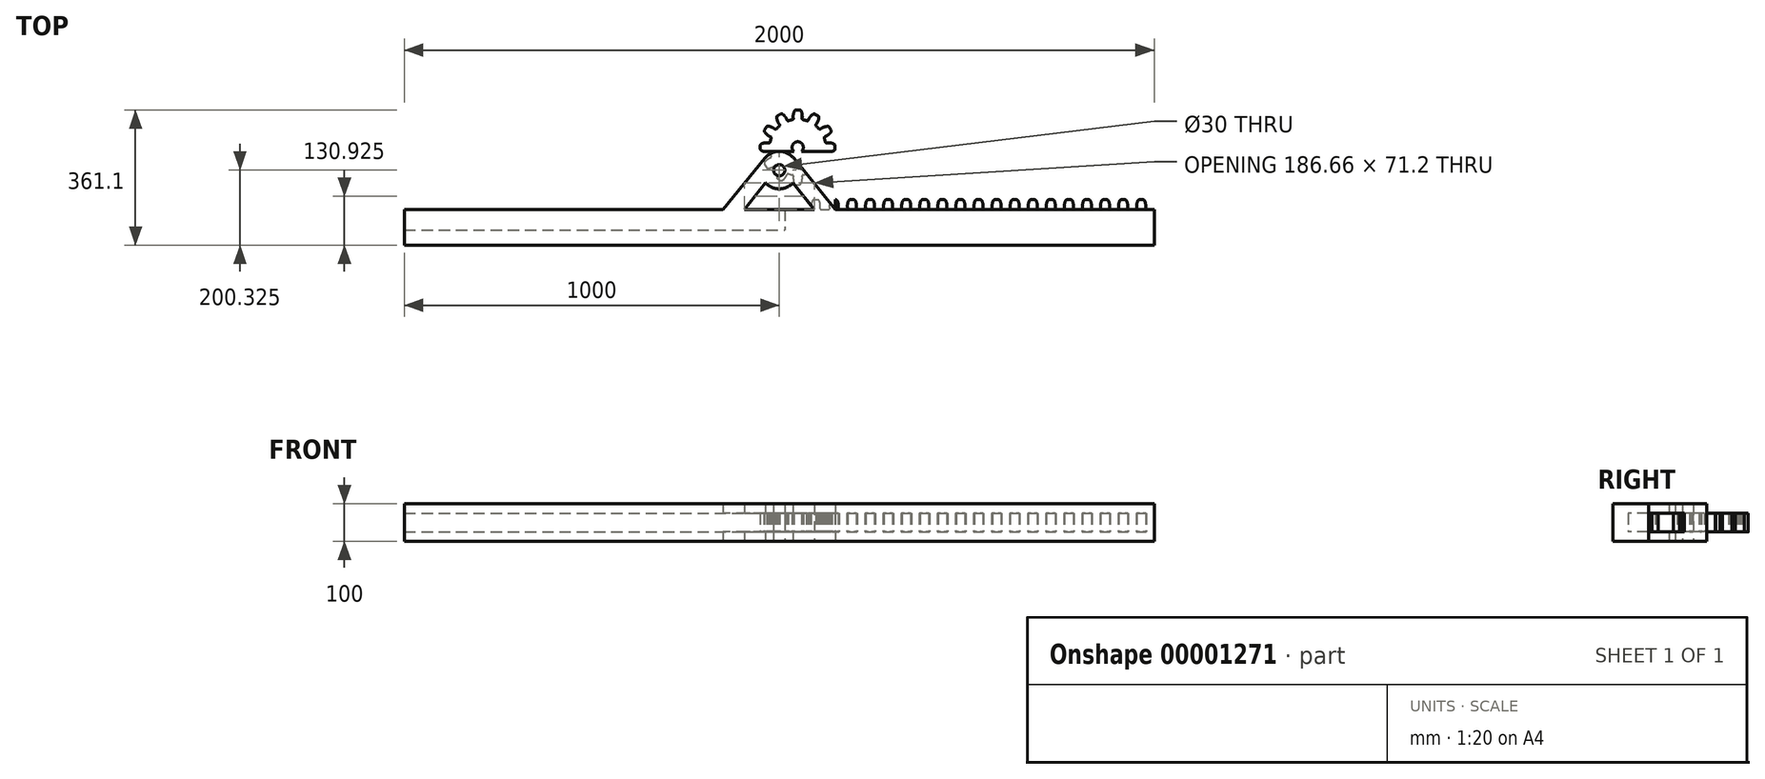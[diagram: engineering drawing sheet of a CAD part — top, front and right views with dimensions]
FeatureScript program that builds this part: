
annotation { "Feature Type Name" : "Feature", "Feature Type Description" : "" }
export const myFeature = defineFeature(function(context is Context, id is Id, definition is map)
    precondition{}
    {
        {
            var Q0;
            Q0=qCreatedBy(makeId("Top.planeOp"),FACE);
            var sketch = newSketch(context, id + "F0", { "sketchPlane" : qUnion([Q0])});
            skLineSegment(sketch, "E0", {"start": v(99.73, 0) * mm, "end": v(99.73, 4.1) * mm});
            skLineSegment(sketch, "E1", {"start": v(99.73, 4.1) * mm, "end": v(99.73, 0) * mm, "construction": true});
            skLineSegment(sketch, "E2", {"start": v(99.73, -4.64) * mm, "end": v(99.73, 0) * mm});
            skPoint(sketch, "E3.center", {"position": v(0, 0) * mm});
            skArc(sketch, "E4.0.MirrorCS", {"start": v(82.68, 12.2) * mm, "mid": v(90.04, 11.17) * mm, "end": v(97, 8.55) * mm});
            skArc(sketch, "E4.1.MirrorCS", {"start": v(76.7, 11.75) * mm, "mid": v(79.67, 12.26) * mm, "end": v(82.68, 12.2) * mm});
            skArc(sketch, "E5", {"start": v(73.52, 14.03) * mm, "mid": v(74.77, 12.37) * mm, "end": v(76.76, 11.75) * mm});
            skPoint(sketch, "E6.end.orphan", {"position": v(82.71, -12.06) * mm});
            skArc(sketch, "E7.0.MirrorCS", {"start": v(82.71, -12.06) * mm, "mid": v(89.87, -11.39) * mm, "end": v(96.73, -9.23) * mm});
            skArc(sketch, "E7.1.MirrorCS", {"start": v(76.73, -11.6) * mm, "mid": v(79.7, -12.11) * mm, "end": v(82.71, -12.06) * mm});
            skArc(sketch, "E7.2.MirrorCS", {"start": v(73.6, -13.73) * mm, "mid": v(74.87, -12.18) * mm, "end": v(76.79, -11.6) * mm});
            skLineSegment(sketch, "E8", {"start": v(-86.47, -119.82) * mm, "end": v(48.54, -119.82) * mm, "construction": true});
            skArc(sketch, "E9.2.MirrorCS", {"start": v(-13.73, -166.04) * mm, "mid": v(-12.2, -164.8) * mm, "end": v(-11.6, -162.91) * mm});
            skArc(sketch, "E9.7.MirrorCS", {"start": v(-12.06, -156.94) * mm, "mid": v(-11.39, -149.78) * mm, "end": v(-9.23, -142.92) * mm});
            skLineSegment(sketch, "E10", {"start": v(0, -139.92) * mm, "end": v(0, -175.01) * mm, "construction": true});
            skArc(sketch, "E11.1.MirrorCS", {"start": v(12.05, -156.94) * mm, "mid": v(11.38, -149.78) * mm, "end": v(9.22, -142.92) * mm});
            skArc(sketch, "E11.2.MirrorCS", {"start": v(13.72, -166.04) * mm, "mid": v(12.18, -164.78) * mm, "end": v(11.6, -162.86) * mm});
            skLineSegment(sketch, "E12", {"start": v(-4.64, -139.92) * mm, "end": v(4.64, -139.92) * mm});
            skArc(sketch, "E13.filletArc", {"start": v(-4.64, -139.92) * mm, "mid": v(-7.38, -140.73) * mm, "end": v(-9.23, -142.92) * mm});
            skArc(sketch, "E14.filletArc", {"start": v(9.22, -142.92) * mm, "mid": v(7.38, -140.73) * mm, "end": v(4.64, -139.92) * mm});
            skArc(sketch, "E15.trimOffspring", {"start": v(70.64, -24.92) * mm, "mid": v(72.37, -19.3) * mm, "end": v(73.67, -13.58) * mm});
            skLineSegment(sketch, "E16", {"start": v(-13.73, -166.04) * mm, "end": v(-34.8, -166.04) * mm});
            skLineSegment(sketch, "E17", {"start": v(950.75, -220.54) * mm, "end": v(-34.8, -220.54) * mm});
            skLineSegment(sketch, "E18", {"start": v(-34.8, -166.04) * mm, "end": v(-34.8, -220.54) * mm});
            skArc(sketch, "E19", {"start": v(-12.06, -156.94) * mm, "mid": v(-11.94, -159.93) * mm, "end": v(-11.6, -162.91) * mm});
            skPoint(sketch, "E11.0.MirrorCS.start.orphan", {"position": v(11.6, -162.91) * mm});
            skArc(sketch, "E20.0.MirrorCS", {"start": v(12.05, -156.94) * mm, "mid": v(11.94, -159.93) * mm, "end": v(11.6, -162.91) * mm});
            skPoint(sketch, "E21.0.MirrorP", {"position": v(-11.6, -162.91) * mm});
            skLineSegment(sketch, "E22", {"start": v(-12.06, -156.94) * mm, "end": v(12.05, -156.94) * mm, "construction": true});
            skLineSegment(sketch, "E23", {"start": v(12.05, -156.94) * mm, "end": v(36.17, -156.94) * mm, "construction": true});
            skLineSegment(sketch, "E24", {"start": v(13.72, -166.04) * mm, "end": v(34.5, -166.04) * mm});
            skPoint(sketch, "E25.visualSharp", {"position": v(99.73, 7) * mm});
            skArc(sketch, "E25.filletArc", {"start": v(99.73, 4.1) * mm, "mid": v(99, 6.7) * mm, "end": v(97, 8.55) * mm});
            skPoint(sketch, "E26.visualSharp", {"position": v(99.73, -7.74) * mm});
            skArc(sketch, "E26.filletArc", {"start": v(96.73, -9.23) * mm, "mid": v(98.91, -7.38) * mm, "end": v(99.73, -4.64) * mm});
            skArc(sketch, "E27.1.0.0", {"start": v(60.28, -156.94) * mm, "mid": v(60.16, -159.93) * mm, "end": v(59.83, -162.91) * mm});
            skLineSegment(sketch, "E27.1.0.1", {"start": v(61.95, -166.04) * mm, "end": v(82.72, -166.04) * mm});
            skArc(sketch, "E27.1.0.2", {"start": v(61.95, -166.04) * mm, "mid": v(60.4, -164.78) * mm, "end": v(59.83, -162.86) * mm});
            skArc(sketch, "E27.1.0.3", {"start": v(36.17, -156.94) * mm, "mid": v(36.28, -159.93) * mm, "end": v(36.62, -162.91) * mm});
            skArc(sketch, "E27.1.0.4", {"start": v(36.17, -156.94) * mm, "mid": v(36.84, -149.78) * mm, "end": v(39, -142.92) * mm});
            skArc(sketch, "E27.1.0.5", {"start": v(34.5, -166.04) * mm, "mid": v(36.03, -164.8) * mm, "end": v(36.62, -162.91) * mm});
            skArc(sketch, "E27.1.0.6", {"start": v(60.28, -156.94) * mm, "mid": v(59.6, -149.78) * mm, "end": v(57.44, -142.92) * mm});
            skPoint(sketch, "E27.1.0.7", {"position": v(36.62, -162.91) * mm});
            skLineSegment(sketch, "E27.1.0.8", {"start": v(43.58, -139.92) * mm, "end": v(52.86, -139.92) * mm});
            skArc(sketch, "E27.1.0.9", {"start": v(43.58, -139.92) * mm, "mid": v(40.84, -140.73) * mm, "end": v(39, -142.92) * mm});
            skPoint(sketch, "E27.1.0.10", {"position": v(59.83, -162.91) * mm});
            skArc(sketch, "E27.1.0.11", {"start": v(57.44, -142.92) * mm, "mid": v(55.6, -140.73) * mm, "end": v(52.86, -139.92) * mm});
            skArc(sketch, "E27.1.0.12", {"start": v(60.28, -156.94) * mm, "mid": v(60.16, -159.93) * mm, "end": v(59.83, -162.91) * mm});
            skArc(sketch, "E27.1.0.13", {"start": v(36.17, -156.94) * mm, "mid": v(36.84, -149.78) * mm, "end": v(39, -142.92) * mm});
            skArc(sketch, "E27.2.0.0", {"start": v(108.5, -156.94) * mm, "mid": v(108.39, -159.93) * mm, "end": v(108.05, -162.91) * mm});
            skLineSegment(sketch, "E27.2.0.1", {"start": v(110.17, -166.04) * mm, "end": v(130.94, -166.04) * mm});
            skArc(sketch, "E27.2.0.2", {"start": v(110.17, -166.04) * mm, "mid": v(108.62, -164.78) * mm, "end": v(108.05, -162.86) * mm});
            skArc(sketch, "E27.2.0.3", {"start": v(84.39, -156.94) * mm, "mid": v(84.5, -159.93) * mm, "end": v(84.84, -162.91) * mm});
            skArc(sketch, "E27.2.0.4", {"start": v(84.39, -156.94) * mm, "mid": v(85.06, -149.78) * mm, "end": v(87.22, -142.92) * mm});
            skArc(sketch, "E27.2.0.5", {"start": v(82.72, -166.04) * mm, "mid": v(84.25, -164.8) * mm, "end": v(84.84, -162.91) * mm});
            skArc(sketch, "E27.2.0.6", {"start": v(108.5, -156.94) * mm, "mid": v(107.83, -149.78) * mm, "end": v(105.67, -142.92) * mm});
            skPoint(sketch, "E27.2.0.7", {"position": v(84.84, -162.91) * mm});
            skLineSegment(sketch, "E27.2.0.8", {"start": v(91.8, -139.92) * mm, "end": v(101.09, -139.92) * mm});
            skArc(sketch, "E27.2.0.9", {"start": v(91.8, -139.92) * mm, "mid": v(89.07, -140.73) * mm, "end": v(87.22, -142.92) * mm});
            skPoint(sketch, "E27.2.0.10", {"position": v(108.05, -162.91) * mm});
            skArc(sketch, "E27.2.0.11", {"start": v(105.67, -142.92) * mm, "mid": v(103.82, -140.73) * mm, "end": v(101.09, -139.92) * mm});
            skArc(sketch, "E27.2.0.12", {"start": v(108.5, -156.94) * mm, "mid": v(108.39, -159.93) * mm, "end": v(108.05, -162.91) * mm});
            skArc(sketch, "E27.2.0.13", {"start": v(84.39, -156.94) * mm, "mid": v(85.06, -149.78) * mm, "end": v(87.22, -142.92) * mm});
            skArc(sketch, "E27.3.0.0", {"start": v(156.73, -156.94) * mm, "mid": v(156.61, -159.93) * mm, "end": v(156.27, -162.91) * mm});
            skLineSegment(sketch, "E27.3.0.1", {"start": v(158.4, -166.04) * mm, "end": v(179.17, -166.04) * mm});
            skArc(sketch, "E27.3.0.2", {"start": v(158.4, -166.04) * mm, "mid": v(156.85, -164.78) * mm, "end": v(156.27, -162.86) * mm});
            skArc(sketch, "E27.3.0.3", {"start": v(132.61, -156.94) * mm, "mid": v(132.73, -159.93) * mm, "end": v(133.07, -162.91) * mm});
            skArc(sketch, "E27.3.0.4", {"start": v(132.61, -156.94) * mm, "mid": v(133.28, -149.78) * mm, "end": v(135.45, -142.92) * mm});
            skArc(sketch, "E27.3.0.5", {"start": v(130.94, -166.04) * mm, "mid": v(132.48, -164.8) * mm, "end": v(133.07, -162.91) * mm});
            skArc(sketch, "E27.3.0.6", {"start": v(156.73, -156.94) * mm, "mid": v(156.06, -149.78) * mm, "end": v(153.9, -142.92) * mm});
            skPoint(sketch, "E27.3.0.7", {"position": v(133.07, -162.91) * mm});
            skLineSegment(sketch, "E27.3.0.8", {"start": v(140.03, -139.92) * mm, "end": v(149.31, -139.92) * mm});
            skArc(sketch, "E27.3.0.9", {"start": v(140.03, -139.92) * mm, "mid": v(137.3, -140.73) * mm, "end": v(135.45, -142.92) * mm});
            skPoint(sketch, "E27.3.0.10", {"position": v(156.27, -162.91) * mm});
            skArc(sketch, "E27.3.0.11", {"start": v(153.9, -142.92) * mm, "mid": v(152.05, -140.73) * mm, "end": v(149.31, -139.92) * mm});
            skArc(sketch, "E27.3.0.12", {"start": v(156.73, -156.94) * mm, "mid": v(156.61, -159.93) * mm, "end": v(156.27, -162.91) * mm});
            skArc(sketch, "E27.3.0.13", {"start": v(132.61, -156.94) * mm, "mid": v(133.28, -149.78) * mm, "end": v(135.45, -142.92) * mm});
            skArc(sketch, "E27.4.0.0", {"start": v(204.95, -156.94) * mm, "mid": v(204.84, -159.93) * mm, "end": v(204.5, -162.91) * mm});
            skLineSegment(sketch, "E27.4.0.1", {"start": v(206.62, -166.04) * mm, "end": v(227.4, -166.04) * mm});
            skArc(sketch, "E27.4.0.2", {"start": v(206.62, -166.04) * mm, "mid": v(205.07, -164.78) * mm, "end": v(204.5, -162.86) * mm});
            skArc(sketch, "E27.4.0.3", {"start": v(180.84, -156.94) * mm, "mid": v(180.95, -159.93) * mm, "end": v(181.3, -162.91) * mm});
            skArc(sketch, "E27.4.0.4", {"start": v(180.84, -156.94) * mm, "mid": v(181.5, -149.78) * mm, "end": v(183.67, -142.92) * mm});
            skArc(sketch, "E27.4.0.5", {"start": v(179.17, -166.04) * mm, "mid": v(180.7, -164.8) * mm, "end": v(181.3, -162.91) * mm});
            skArc(sketch, "E27.4.0.6", {"start": v(204.95, -156.94) * mm, "mid": v(204.28, -149.78) * mm, "end": v(202.12, -142.92) * mm});
            skPoint(sketch, "E27.4.0.7", {"position": v(181.3, -162.91) * mm});
            skLineSegment(sketch, "E27.4.0.8", {"start": v(188.25, -139.92) * mm, "end": v(197.53, -139.92) * mm});
            skArc(sketch, "E27.4.0.9", {"start": v(188.25, -139.92) * mm, "mid": v(185.51, -140.73) * mm, "end": v(183.67, -142.92) * mm});
            skPoint(sketch, "E27.4.0.10", {"position": v(204.5, -162.91) * mm});
            skArc(sketch, "E27.4.0.11", {"start": v(202.12, -142.92) * mm, "mid": v(200.27, -140.73) * mm, "end": v(197.53, -139.92) * mm});
            skArc(sketch, "E27.4.0.12", {"start": v(204.95, -156.94) * mm, "mid": v(204.84, -159.93) * mm, "end": v(204.5, -162.91) * mm});
            skArc(sketch, "E27.4.0.13", {"start": v(180.84, -156.94) * mm, "mid": v(181.5, -149.78) * mm, "end": v(183.67, -142.92) * mm});
            skArc(sketch, "E27.5.0.0", {"start": v(253.17, -156.94) * mm, "mid": v(253.06, -159.93) * mm, "end": v(252.72, -162.91) * mm});
            skLineSegment(sketch, "E27.5.0.1", {"start": v(254.84, -166.04) * mm, "end": v(275.62, -166.04) * mm});
            skArc(sketch, "E27.5.0.2", {"start": v(254.84, -166.04) * mm, "mid": v(253.3, -164.78) * mm, "end": v(252.72, -162.86) * mm});
            skArc(sketch, "E27.5.0.3", {"start": v(229.06, -156.94) * mm, "mid": v(229.18, -159.93) * mm, "end": v(229.51, -162.91) * mm});
            skArc(sketch, "E27.5.0.4", {"start": v(229.06, -156.94) * mm, "mid": v(229.73, -149.78) * mm, "end": v(231.9, -142.92) * mm});
            skArc(sketch, "E27.5.0.5", {"start": v(227.4, -166.04) * mm, "mid": v(228.92, -164.8) * mm, "end": v(229.51, -162.91) * mm});
            skArc(sketch, "E27.5.0.6", {"start": v(253.17, -156.94) * mm, "mid": v(252.5, -149.78) * mm, "end": v(250.34, -142.92) * mm});
            skPoint(sketch, "E27.5.0.7", {"position": v(229.51, -162.91) * mm});
            skLineSegment(sketch, "E27.5.0.8", {"start": v(236.48, -139.92) * mm, "end": v(245.76, -139.92) * mm});
            skArc(sketch, "E27.5.0.9", {"start": v(236.48, -139.92) * mm, "mid": v(233.74, -140.73) * mm, "end": v(231.9, -142.92) * mm});
            skPoint(sketch, "E27.5.0.10", {"position": v(252.72, -162.91) * mm});
            skArc(sketch, "E27.5.0.11", {"start": v(250.34, -142.92) * mm, "mid": v(248.5, -140.73) * mm, "end": v(245.76, -139.92) * mm});
            skArc(sketch, "E27.5.0.12", {"start": v(253.17, -156.94) * mm, "mid": v(253.06, -159.93) * mm, "end": v(252.72, -162.91) * mm});
            skArc(sketch, "E27.5.0.13", {"start": v(229.06, -156.94) * mm, "mid": v(229.73, -149.78) * mm, "end": v(231.9, -142.92) * mm});
            skArc(sketch, "E27.6.0.0", {"start": v(301.4, -156.94) * mm, "mid": v(301.28, -159.93) * mm, "end": v(300.95, -162.91) * mm});
            skLineSegment(sketch, "E27.6.0.1", {"start": v(303.07, -166.04) * mm, "end": v(323.84, -166.04) * mm});
            skArc(sketch, "E27.6.0.2", {"start": v(303.07, -166.04) * mm, "mid": v(301.52, -164.78) * mm, "end": v(300.95, -162.86) * mm});
            skArc(sketch, "E27.6.0.3", {"start": v(277.29, -156.94) * mm, "mid": v(277.4, -159.93) * mm, "end": v(277.74, -162.91) * mm});
            skArc(sketch, "E27.6.0.4", {"start": v(277.29, -156.94) * mm, "mid": v(277.96, -149.78) * mm, "end": v(280.12, -142.92) * mm});
            skArc(sketch, "E27.6.0.5", {"start": v(275.62, -166.04) * mm, "mid": v(277.15, -164.8) * mm, "end": v(277.74, -162.91) * mm});
            skArc(sketch, "E27.6.0.6", {"start": v(301.4, -156.94) * mm, "mid": v(300.73, -149.78) * mm, "end": v(298.56, -142.92) * mm});
            skPoint(sketch, "E27.6.0.7", {"position": v(277.74, -162.91) * mm});
            skLineSegment(sketch, "E27.6.0.8", {"start": v(284.7, -139.92) * mm, "end": v(293.98, -139.92) * mm});
            skArc(sketch, "E27.6.0.9", {"start": v(284.7, -139.92) * mm, "mid": v(281.96, -140.73) * mm, "end": v(280.12, -142.92) * mm});
            skPoint(sketch, "E27.6.0.10", {"position": v(300.95, -162.91) * mm});
            skArc(sketch, "E27.6.0.11", {"start": v(298.56, -142.92) * mm, "mid": v(296.72, -140.73) * mm, "end": v(293.98, -139.92) * mm});
            skArc(sketch, "E27.6.0.12", {"start": v(301.4, -156.94) * mm, "mid": v(301.28, -159.93) * mm, "end": v(300.95, -162.91) * mm});
            skArc(sketch, "E27.6.0.13", {"start": v(277.29, -156.94) * mm, "mid": v(277.96, -149.78) * mm, "end": v(280.12, -142.92) * mm});
            skArc(sketch, "E27.7.0.0", {"start": v(349.62, -156.94) * mm, "mid": v(349.5, -159.93) * mm, "end": v(349.17, -162.91) * mm});
            skLineSegment(sketch, "E27.7.0.1", {"start": v(351.3, -166.04) * mm, "end": v(372.06, -166.04) * mm});
            skArc(sketch, "E27.7.0.2", {"start": v(351.3, -166.04) * mm, "mid": v(349.74, -164.78) * mm, "end": v(349.17, -162.86) * mm});
            skArc(sketch, "E27.7.0.3", {"start": v(325.5, -156.94) * mm, "mid": v(325.62, -159.93) * mm, "end": v(325.96, -162.91) * mm});
            skArc(sketch, "E27.7.0.4", {"start": v(325.5, -156.94) * mm, "mid": v(326.18, -149.78) * mm, "end": v(328.34, -142.92) * mm});
            skArc(sketch, "E27.7.0.5", {"start": v(323.84, -166.04) * mm, "mid": v(325.37, -164.8) * mm, "end": v(325.96, -162.91) * mm});
            skArc(sketch, "E27.7.0.6", {"start": v(349.62, -156.94) * mm, "mid": v(348.95, -149.78) * mm, "end": v(346.79, -142.92) * mm});
            skPoint(sketch, "E27.7.0.7", {"position": v(325.96, -162.91) * mm});
            skLineSegment(sketch, "E27.7.0.8", {"start": v(332.93, -139.92) * mm, "end": v(342.2, -139.92) * mm});
            skArc(sketch, "E27.7.0.9", {"start": v(332.93, -139.92) * mm, "mid": v(330.19, -140.73) * mm, "end": v(328.34, -142.92) * mm});
            skPoint(sketch, "E27.7.0.10", {"position": v(349.17, -162.91) * mm});
            skArc(sketch, "E27.7.0.11", {"start": v(346.79, -142.92) * mm, "mid": v(344.94, -140.73) * mm, "end": v(342.2, -139.92) * mm});
            skArc(sketch, "E27.7.0.12", {"start": v(349.62, -156.94) * mm, "mid": v(349.5, -159.93) * mm, "end": v(349.17, -162.91) * mm});
            skArc(sketch, "E27.7.0.13", {"start": v(325.5, -156.94) * mm, "mid": v(326.18, -149.78) * mm, "end": v(328.34, -142.92) * mm});
            skArc(sketch, "E27.8.0.0", {"start": v(397.85, -156.94) * mm, "mid": v(397.73, -159.93) * mm, "end": v(397.4, -162.91) * mm});
            skLineSegment(sketch, "E27.8.0.1", {"start": v(399.52, -166.04) * mm, "end": v(420.29, -166.04) * mm});
            skArc(sketch, "E27.8.0.2", {"start": v(399.52, -166.04) * mm, "mid": v(397.97, -164.78) * mm, "end": v(397.4, -162.86) * mm});
            skArc(sketch, "E27.8.0.3", {"start": v(373.73, -156.94) * mm, "mid": v(373.85, -159.93) * mm, "end": v(374.19, -162.91) * mm});
            skArc(sketch, "E27.8.0.4", {"start": v(373.73, -156.94) * mm, "mid": v(374.4, -149.78) * mm, "end": v(376.57, -142.92) * mm});
            skArc(sketch, "E27.8.0.5", {"start": v(372.06, -166.04) * mm, "mid": v(373.6, -164.8) * mm, "end": v(374.19, -162.91) * mm});
            skArc(sketch, "E27.8.0.6", {"start": v(397.85, -156.94) * mm, "mid": v(397.18, -149.78) * mm, "end": v(395.01, -142.92) * mm});
            skPoint(sketch, "E27.8.0.7", {"position": v(374.19, -162.91) * mm});
            skLineSegment(sketch, "E27.8.0.8", {"start": v(381.15, -139.92) * mm, "end": v(390.43, -139.92) * mm});
            skArc(sketch, "E27.8.0.9", {"start": v(381.15, -139.92) * mm, "mid": v(378.41, -140.73) * mm, "end": v(376.57, -142.92) * mm});
            skPoint(sketch, "E27.8.0.10", {"position": v(397.4, -162.91) * mm});
            skArc(sketch, "E27.8.0.11", {"start": v(395.01, -142.92) * mm, "mid": v(393.17, -140.73) * mm, "end": v(390.43, -139.92) * mm});
            skArc(sketch, "E27.8.0.12", {"start": v(397.85, -156.94) * mm, "mid": v(397.73, -159.93) * mm, "end": v(397.4, -162.91) * mm});
            skArc(sketch, "E27.8.0.13", {"start": v(373.73, -156.94) * mm, "mid": v(374.4, -149.78) * mm, "end": v(376.57, -142.92) * mm});
            skArc(sketch, "E27.9.0.0", {"start": v(446.07, -156.94) * mm, "mid": v(445.96, -159.93) * mm, "end": v(445.62, -162.91) * mm});
            skLineSegment(sketch, "E27.9.0.1", {"start": v(447.74, -166.04) * mm, "end": v(468.51, -166.04) * mm});
            skArc(sketch, "E27.9.0.2", {"start": v(447.74, -166.04) * mm, "mid": v(446.2, -164.78) * mm, "end": v(445.62, -162.86) * mm});
            skArc(sketch, "E27.9.0.3", {"start": v(421.96, -156.94) * mm, "mid": v(422.07, -159.93) * mm, "end": v(422.41, -162.91) * mm});
            skArc(sketch, "E27.9.0.4", {"start": v(421.96, -156.94) * mm, "mid": v(422.63, -149.78) * mm, "end": v(424.8, -142.92) * mm});
            skArc(sketch, "E27.9.0.5", {"start": v(420.29, -166.04) * mm, "mid": v(421.82, -164.8) * mm, "end": v(422.41, -162.91) * mm});
            skArc(sketch, "E27.9.0.6", {"start": v(446.07, -156.94) * mm, "mid": v(445.4, -149.78) * mm, "end": v(443.24, -142.92) * mm});
            skPoint(sketch, "E27.9.0.7", {"position": v(422.41, -162.91) * mm});
            skLineSegment(sketch, "E27.9.0.8", {"start": v(429.37, -139.92) * mm, "end": v(438.65, -139.92) * mm});
            skArc(sketch, "E27.9.0.9", {"start": v(429.37, -139.92) * mm, "mid": v(426.63, -140.73) * mm, "end": v(424.8, -142.92) * mm});
            skPoint(sketch, "E27.9.0.10", {"position": v(445.62, -162.91) * mm});
            skArc(sketch, "E27.9.0.11", {"start": v(443.24, -142.92) * mm, "mid": v(441.4, -140.73) * mm, "end": v(438.65, -139.92) * mm});
            skArc(sketch, "E27.9.0.12", {"start": v(446.07, -156.94) * mm, "mid": v(445.96, -159.93) * mm, "end": v(445.62, -162.91) * mm});
            skArc(sketch, "E27.9.0.13", {"start": v(421.96, -156.94) * mm, "mid": v(422.63, -149.78) * mm, "end": v(424.8, -142.92) * mm});
            skArc(sketch, "E27.10.0.0", {"start": v(494.3, -156.94) * mm, "mid": v(494.18, -159.93) * mm, "end": v(493.84, -162.91) * mm});
            skLineSegment(sketch, "E27.10.0.1", {"start": v(495.96, -166.04) * mm, "end": v(516.74, -166.04) * mm});
            skArc(sketch, "E27.10.0.2", {"start": v(495.96, -166.04) * mm, "mid": v(494.42, -164.78) * mm, "end": v(493.84, -162.86) * mm});
            skArc(sketch, "E27.10.0.3", {"start": v(470.18, -156.94) * mm, "mid": v(470.3, -159.93) * mm, "end": v(470.63, -162.91) * mm});
            skArc(sketch, "E27.10.0.4", {"start": v(470.18, -156.94) * mm, "mid": v(470.85, -149.78) * mm, "end": v(473.01, -142.92) * mm});
            skArc(sketch, "E27.10.0.5", {"start": v(468.51, -166.04) * mm, "mid": v(470.04, -164.8) * mm, "end": v(470.63, -162.91) * mm});
            skArc(sketch, "E27.10.0.6", {"start": v(494.3, -156.94) * mm, "mid": v(493.62, -149.78) * mm, "end": v(491.46, -142.92) * mm});
            skPoint(sketch, "E27.10.0.7", {"position": v(470.63, -162.91) * mm});
            skLineSegment(sketch, "E27.10.0.8", {"start": v(477.6, -139.92) * mm, "end": v(486.88, -139.92) * mm});
            skArc(sketch, "E27.10.0.9", {"start": v(477.6, -139.92) * mm, "mid": v(474.86, -140.73) * mm, "end": v(473.01, -142.92) * mm});
            skPoint(sketch, "E27.10.0.10", {"position": v(493.84, -162.91) * mm});
            skArc(sketch, "E27.10.0.11", {"start": v(491.46, -142.92) * mm, "mid": v(489.62, -140.73) * mm, "end": v(486.88, -139.92) * mm});
            skArc(sketch, "E27.10.0.12", {"start": v(494.3, -156.94) * mm, "mid": v(494.18, -159.93) * mm, "end": v(493.84, -162.91) * mm});
            skArc(sketch, "E27.10.0.13", {"start": v(470.18, -156.94) * mm, "mid": v(470.85, -149.78) * mm, "end": v(473.01, -142.92) * mm});
            skArc(sketch, "E27.11.0.0", {"start": v(542.52, -156.94) * mm, "mid": v(542.4, -159.93) * mm, "end": v(542.07, -162.91) * mm});
            skLineSegment(sketch, "E27.11.0.1", {"start": v(544.19, -166.04) * mm, "end": v(564.96, -166.04) * mm});
            skArc(sketch, "E27.11.0.2", {"start": v(544.19, -166.04) * mm, "mid": v(542.64, -164.78) * mm, "end": v(542.07, -162.86) * mm});
            skArc(sketch, "E27.11.0.3", {"start": v(518.4, -156.94) * mm, "mid": v(518.52, -159.93) * mm, "end": v(518.86, -162.91) * mm});
            skArc(sketch, "E27.11.0.4", {"start": v(518.4, -156.94) * mm, "mid": v(519.08, -149.78) * mm, "end": v(521.24, -142.92) * mm});
            skArc(sketch, "E27.11.0.5", {"start": v(516.74, -166.04) * mm, "mid": v(518.27, -164.8) * mm, "end": v(518.86, -162.91) * mm});
            skArc(sketch, "E27.11.0.6", {"start": v(542.52, -156.94) * mm, "mid": v(541.85, -149.78) * mm, "end": v(539.68, -142.92) * mm});
            skPoint(sketch, "E27.11.0.7", {"position": v(518.86, -162.91) * mm});
            skLineSegment(sketch, "E27.11.0.8", {"start": v(525.82, -139.92) * mm, "end": v(535.1, -139.92) * mm});
            skArc(sketch, "E27.11.0.9", {"start": v(525.82, -139.92) * mm, "mid": v(523.08, -140.73) * mm, "end": v(521.24, -142.92) * mm});
            skPoint(sketch, "E27.11.0.10", {"position": v(542.07, -162.91) * mm});
            skArc(sketch, "E27.11.0.11", {"start": v(539.68, -142.92) * mm, "mid": v(537.84, -140.73) * mm, "end": v(535.1, -139.92) * mm});
            skArc(sketch, "E27.11.0.12", {"start": v(542.52, -156.94) * mm, "mid": v(542.4, -159.93) * mm, "end": v(542.07, -162.91) * mm});
            skArc(sketch, "E27.11.0.13", {"start": v(518.4, -156.94) * mm, "mid": v(519.08, -149.78) * mm, "end": v(521.24, -142.92) * mm});
            skArc(sketch, "E27.12.0.0", {"start": v(590.74, -156.94) * mm, "mid": v(590.63, -159.93) * mm, "end": v(590.29, -162.91) * mm});
            skLineSegment(sketch, "E27.12.0.1", {"start": v(592.41, -166.04) * mm, "end": v(613.18, -166.04) * mm});
            skArc(sketch, "E27.12.0.2", {"start": v(592.41, -166.04) * mm, "mid": v(590.86, -164.78) * mm, "end": v(590.29, -162.86) * mm});
            skArc(sketch, "E27.12.0.3", {"start": v(566.63, -156.94) * mm, "mid": v(566.74, -159.93) * mm, "end": v(567.08, -162.91) * mm});
            skArc(sketch, "E27.12.0.4", {"start": v(566.63, -156.94) * mm, "mid": v(567.3, -149.78) * mm, "end": v(569.46, -142.92) * mm});
            skArc(sketch, "E27.12.0.5", {"start": v(564.96, -166.04) * mm, "mid": v(566.5, -164.8) * mm, "end": v(567.08, -162.91) * mm});
            skArc(sketch, "E27.12.0.6", {"start": v(590.74, -156.94) * mm, "mid": v(590.07, -149.78) * mm, "end": v(587.9, -142.92) * mm});
            skPoint(sketch, "E27.12.0.7", {"position": v(567.08, -162.91) * mm});
            skLineSegment(sketch, "E27.12.0.8", {"start": v(574.05, -139.92) * mm, "end": v(583.33, -139.92) * mm});
            skArc(sketch, "E27.12.0.9", {"start": v(574.05, -139.92) * mm, "mid": v(571.3, -140.73) * mm, "end": v(569.46, -142.92) * mm});
            skPoint(sketch, "E27.12.0.10", {"position": v(590.29, -162.91) * mm});
            skArc(sketch, "E27.12.0.11", {"start": v(587.9, -142.92) * mm, "mid": v(586.06, -140.73) * mm, "end": v(583.33, -139.92) * mm});
            skArc(sketch, "E27.12.0.12", {"start": v(590.74, -156.94) * mm, "mid": v(590.63, -159.93) * mm, "end": v(590.29, -162.91) * mm});
            skArc(sketch, "E27.12.0.13", {"start": v(566.63, -156.94) * mm, "mid": v(567.3, -149.78) * mm, "end": v(569.46, -142.92) * mm});
            skArc(sketch, "E27.13.0.0", {"start": v(638.97, -156.94) * mm, "mid": v(638.85, -159.93) * mm, "end": v(638.51, -162.91) * mm});
            skLineSegment(sketch, "E27.13.0.1", {"start": v(640.64, -166.04) * mm, "end": v(661.4, -166.04) * mm});
            skArc(sketch, "E27.13.0.2", {"start": v(640.64, -166.04) * mm, "mid": v(639.09, -164.78) * mm, "end": v(638.51, -162.86) * mm});
            skArc(sketch, "E27.13.0.3", {"start": v(614.85, -156.94) * mm, "mid": v(614.97, -159.93) * mm, "end": v(615.3, -162.91) * mm});
            skArc(sketch, "E27.13.0.4", {"start": v(614.85, -156.94) * mm, "mid": v(615.52, -149.78) * mm, "end": v(617.69, -142.92) * mm});
            skArc(sketch, "E27.13.0.5", {"start": v(613.18, -166.04) * mm, "mid": v(614.72, -164.8) * mm, "end": v(615.3, -162.91) * mm});
            skArc(sketch, "E27.13.0.6", {"start": v(638.97, -156.94) * mm, "mid": v(638.3, -149.78) * mm, "end": v(636.13, -142.92) * mm});
            skPoint(sketch, "E27.13.0.7", {"position": v(615.3, -162.91) * mm});
            skLineSegment(sketch, "E27.13.0.8", {"start": v(622.27, -139.92) * mm, "end": v(631.55, -139.92) * mm});
            skArc(sketch, "E27.13.0.9", {"start": v(622.27, -139.92) * mm, "mid": v(619.53, -140.73) * mm, "end": v(617.69, -142.92) * mm});
            skPoint(sketch, "E27.13.0.10", {"position": v(638.51, -162.91) * mm});
            skArc(sketch, "E27.13.0.11", {"start": v(636.13, -142.92) * mm, "mid": v(634.29, -140.73) * mm, "end": v(631.55, -139.92) * mm});
            skArc(sketch, "E27.13.0.12", {"start": v(638.97, -156.94) * mm, "mid": v(638.85, -159.93) * mm, "end": v(638.51, -162.91) * mm});
            skArc(sketch, "E27.13.0.13", {"start": v(614.85, -156.94) * mm, "mid": v(615.52, -149.78) * mm, "end": v(617.69, -142.92) * mm});
            skArc(sketch, "E27.14.0.0", {"start": v(687.19, -156.94) * mm, "mid": v(687.08, -159.93) * mm, "end": v(686.74, -162.91) * mm});
            skLineSegment(sketch, "E27.14.0.1", {"start": v(688.86, -166.04) * mm, "end": v(709.63, -166.04) * mm});
            skArc(sketch, "E27.14.0.2", {"start": v(688.86, -166.04) * mm, "mid": v(687.31, -164.78) * mm, "end": v(686.74, -162.86) * mm});
            skArc(sketch, "E27.14.0.3", {"start": v(663.08, -156.94) * mm, "mid": v(663.2, -159.93) * mm, "end": v(663.53, -162.91) * mm});
            skArc(sketch, "E27.14.0.4", {"start": v(663.08, -156.94) * mm, "mid": v(663.75, -149.78) * mm, "end": v(665.91, -142.92) * mm});
            skArc(sketch, "E27.14.0.5", {"start": v(661.4, -166.04) * mm, "mid": v(662.94, -164.8) * mm, "end": v(663.53, -162.91) * mm});
            skArc(sketch, "E27.14.0.6", {"start": v(687.19, -156.94) * mm, "mid": v(686.52, -149.78) * mm, "end": v(684.36, -142.92) * mm});
            skPoint(sketch, "E27.14.0.7", {"position": v(663.53, -162.91) * mm});
            skLineSegment(sketch, "E27.14.0.8", {"start": v(670.5, -139.92) * mm, "end": v(679.77, -139.92) * mm});
            skArc(sketch, "E27.14.0.9", {"start": v(670.5, -139.92) * mm, "mid": v(667.75, -140.73) * mm, "end": v(665.91, -142.92) * mm});
            skPoint(sketch, "E27.14.0.10", {"position": v(686.74, -162.91) * mm});
            skArc(sketch, "E27.14.0.11", {"start": v(684.36, -142.92) * mm, "mid": v(682.51, -140.73) * mm, "end": v(679.77, -139.92) * mm});
            skArc(sketch, "E27.14.0.12", {"start": v(687.19, -156.94) * mm, "mid": v(687.08, -159.93) * mm, "end": v(686.74, -162.91) * mm});
            skArc(sketch, "E27.14.0.13", {"start": v(663.08, -156.94) * mm, "mid": v(663.75, -149.78) * mm, "end": v(665.91, -142.92) * mm});
            skArc(sketch, "E27.15.0.0", {"start": v(735.41, -156.94) * mm, "mid": v(735.3, -159.93) * mm, "end": v(734.96, -162.91) * mm});
            skLineSegment(sketch, "E27.15.0.1", {"start": v(737.08, -166.04) * mm, "end": v(757.86, -166.04) * mm});
            skArc(sketch, "E27.15.0.2", {"start": v(737.08, -166.04) * mm, "mid": v(735.54, -164.78) * mm, "end": v(734.96, -162.86) * mm});
            skArc(sketch, "E27.15.0.3", {"start": v(711.3, -156.94) * mm, "mid": v(711.42, -159.93) * mm, "end": v(711.75, -162.91) * mm});
            skArc(sketch, "E27.15.0.4", {"start": v(711.3, -156.94) * mm, "mid": v(711.97, -149.78) * mm, "end": v(714.13, -142.92) * mm});
            skArc(sketch, "E27.15.0.5", {"start": v(709.63, -166.04) * mm, "mid": v(711.16, -164.8) * mm, "end": v(711.75, -162.91) * mm});
            skArc(sketch, "E27.15.0.6", {"start": v(735.41, -156.94) * mm, "mid": v(734.74, -149.78) * mm, "end": v(732.58, -142.92) * mm});
            skPoint(sketch, "E27.15.0.7", {"position": v(711.75, -162.91) * mm});
            skLineSegment(sketch, "E27.15.0.8", {"start": v(718.72, -139.92) * mm, "end": v(728, -139.92) * mm});
            skArc(sketch, "E27.15.0.9", {"start": v(718.72, -139.92) * mm, "mid": v(715.98, -140.73) * mm, "end": v(714.13, -142.92) * mm});
            skPoint(sketch, "E27.15.0.10", {"position": v(734.96, -162.91) * mm});
            skArc(sketch, "E27.15.0.11", {"start": v(732.58, -142.92) * mm, "mid": v(730.74, -140.73) * mm, "end": v(728, -139.92) * mm});
            skArc(sketch, "E27.15.0.12", {"start": v(735.41, -156.94) * mm, "mid": v(735.3, -159.93) * mm, "end": v(734.96, -162.91) * mm});
            skArc(sketch, "E27.15.0.13", {"start": v(711.3, -156.94) * mm, "mid": v(711.97, -149.78) * mm, "end": v(714.13, -142.92) * mm});
            skArc(sketch, "E27.16.0.0", {"start": v(783.64, -156.94) * mm, "mid": v(783.52, -159.93) * mm, "end": v(783.19, -162.91) * mm});
            skLineSegment(sketch, "E27.16.0.1", {"start": v(785.3, -166.04) * mm, "end": v(806.08, -166.04) * mm});
            skArc(sketch, "E27.16.0.2", {"start": v(785.3, -166.04) * mm, "mid": v(783.76, -164.78) * mm, "end": v(783.19, -162.86) * mm});
            skArc(sketch, "E27.16.0.3", {"start": v(759.53, -156.94) * mm, "mid": v(759.64, -159.93) * mm, "end": v(759.98, -162.91) * mm});
            skArc(sketch, "E27.16.0.4", {"start": v(759.53, -156.94) * mm, "mid": v(760.2, -149.78) * mm, "end": v(762.36, -142.92) * mm});
            skArc(sketch, "E27.16.0.5", {"start": v(757.86, -166.04) * mm, "mid": v(759.39, -164.8) * mm, "end": v(759.98, -162.91) * mm});
            skArc(sketch, "E27.16.0.6", {"start": v(783.64, -156.94) * mm, "mid": v(782.97, -149.78) * mm, "end": v(780.8, -142.92) * mm});
            skPoint(sketch, "E27.16.0.7", {"position": v(759.98, -162.91) * mm});
            skLineSegment(sketch, "E27.16.0.8", {"start": v(766.94, -139.92) * mm, "end": v(776.22, -139.92) * mm});
            skArc(sketch, "E27.16.0.9", {"start": v(766.94, -139.92) * mm, "mid": v(764.2, -140.73) * mm, "end": v(762.36, -142.92) * mm});
            skPoint(sketch, "E27.16.0.10", {"position": v(783.19, -162.91) * mm});
            skArc(sketch, "E27.16.0.11", {"start": v(780.8, -142.92) * mm, "mid": v(778.96, -140.73) * mm, "end": v(776.22, -139.92) * mm});
            skArc(sketch, "E27.16.0.12", {"start": v(783.64, -156.94) * mm, "mid": v(783.52, -159.93) * mm, "end": v(783.19, -162.91) * mm});
            skArc(sketch, "E27.16.0.13", {"start": v(759.53, -156.94) * mm, "mid": v(760.2, -149.78) * mm, "end": v(762.36, -142.92) * mm});
            skArc(sketch, "E27.17.0.0", {"start": v(831.86, -156.94) * mm, "mid": v(831.75, -159.93) * mm, "end": v(831.4, -162.91) * mm});
            skLineSegment(sketch, "E27.17.0.1", {"start": v(833.53, -166.04) * mm, "end": v(854.3, -166.04) * mm});
            skArc(sketch, "E27.17.0.2", {"start": v(833.53, -166.04) * mm, "mid": v(831.98, -164.78) * mm, "end": v(831.4, -162.86) * mm});
            skArc(sketch, "E27.17.0.3", {"start": v(807.75, -156.94) * mm, "mid": v(807.86, -159.93) * mm, "end": v(808.2, -162.91) * mm});
            skArc(sketch, "E27.17.0.4", {"start": v(807.75, -156.94) * mm, "mid": v(808.42, -149.78) * mm, "end": v(810.58, -142.92) * mm});
            skArc(sketch, "E27.17.0.5", {"start": v(806.08, -166.04) * mm, "mid": v(807.61, -164.8) * mm, "end": v(808.2, -162.91) * mm});
            skArc(sketch, "E27.17.0.6", {"start": v(831.86, -156.94) * mm, "mid": v(831.2, -149.78) * mm, "end": v(829.03, -142.92) * mm});
            skPoint(sketch, "E27.17.0.7", {"position": v(808.2, -162.91) * mm});
            skLineSegment(sketch, "E27.17.0.8", {"start": v(815.17, -139.92) * mm, "end": v(824.45, -139.92) * mm});
            skArc(sketch, "E27.17.0.9", {"start": v(815.17, -139.92) * mm, "mid": v(812.43, -140.73) * mm, "end": v(810.58, -142.92) * mm});
            skPoint(sketch, "E27.17.0.10", {"position": v(831.4, -162.91) * mm});
            skArc(sketch, "E27.17.0.11", {"start": v(829.03, -142.92) * mm, "mid": v(827.18, -140.73) * mm, "end": v(824.45, -139.92) * mm});
            skArc(sketch, "E27.17.0.12", {"start": v(831.86, -156.94) * mm, "mid": v(831.75, -159.93) * mm, "end": v(831.4, -162.91) * mm});
            skArc(sketch, "E27.17.0.13", {"start": v(807.75, -156.94) * mm, "mid": v(808.42, -149.78) * mm, "end": v(810.58, -142.92) * mm});
            skArc(sketch, "E27.18.0.0", {"start": v(880.09, -156.94) * mm, "mid": v(879.97, -159.93) * mm, "end": v(879.63, -162.91) * mm});
            skLineSegment(sketch, "E27.18.0.1", {"start": v(881.76, -166.04) * mm, "end": v(902.53, -166.04) * mm});
            skArc(sketch, "E27.18.0.2", {"start": v(881.76, -166.04) * mm, "mid": v(880.2, -164.78) * mm, "end": v(879.63, -162.86) * mm});
            skArc(sketch, "E27.18.0.3", {"start": v(855.97, -156.94) * mm, "mid": v(856.09, -159.93) * mm, "end": v(856.43, -162.91) * mm});
            skArc(sketch, "E27.18.0.4", {"start": v(855.97, -156.94) * mm, "mid": v(856.64, -149.78) * mm, "end": v(858.8, -142.92) * mm});
            skArc(sketch, "E27.18.0.5", {"start": v(854.3, -166.04) * mm, "mid": v(855.84, -164.8) * mm, "end": v(856.43, -162.91) * mm});
            skArc(sketch, "E27.18.0.6", {"start": v(880.09, -156.94) * mm, "mid": v(879.42, -149.78) * mm, "end": v(877.25, -142.92) * mm});
            skPoint(sketch, "E27.18.0.7", {"position": v(856.43, -162.91) * mm});
            skLineSegment(sketch, "E27.18.0.8", {"start": v(863.39, -139.92) * mm, "end": v(872.67, -139.92) * mm});
            skArc(sketch, "E27.18.0.9", {"start": v(863.39, -139.92) * mm, "mid": v(860.65, -140.73) * mm, "end": v(858.8, -142.92) * mm});
            skPoint(sketch, "E27.18.0.10", {"position": v(879.63, -162.91) * mm});
            skArc(sketch, "E27.18.0.11", {"start": v(877.25, -142.92) * mm, "mid": v(875.4, -140.73) * mm, "end": v(872.67, -139.92) * mm});
            skArc(sketch, "E27.18.0.12", {"start": v(880.09, -156.94) * mm, "mid": v(879.97, -159.93) * mm, "end": v(879.63, -162.91) * mm});
            skArc(sketch, "E27.18.0.13", {"start": v(855.97, -156.94) * mm, "mid": v(856.64, -149.78) * mm, "end": v(858.8, -142.92) * mm});
            skArc(sketch, "E27.19.0.0", {"start": v(928.3, -156.94) * mm, "mid": v(928.2, -159.93) * mm, "end": v(927.86, -162.91) * mm});
            skLineSegment(sketch, "E27.19.0.1", {"start": v(929.98, -166.04) * mm, "end": v(950.75, -166.04) * mm});
            skArc(sketch, "E27.19.0.2", {"start": v(929.98, -166.04) * mm, "mid": v(928.43, -164.78) * mm, "end": v(927.86, -162.86) * mm});
            skArc(sketch, "E27.19.0.3", {"start": v(904.2, -156.94) * mm, "mid": v(904.31, -159.93) * mm, "end": v(904.65, -162.91) * mm});
            skArc(sketch, "E27.19.0.4", {"start": v(904.2, -156.94) * mm, "mid": v(904.87, -149.78) * mm, "end": v(907.03, -142.92) * mm});
            skArc(sketch, "E27.19.0.5", {"start": v(902.53, -166.04) * mm, "mid": v(904.06, -164.8) * mm, "end": v(904.65, -162.91) * mm});
            skArc(sketch, "E27.19.0.6", {"start": v(928.3, -156.94) * mm, "mid": v(927.64, -149.78) * mm, "end": v(925.48, -142.92) * mm});
            skPoint(sketch, "E27.19.0.7", {"position": v(904.65, -162.91) * mm});
            skLineSegment(sketch, "E27.19.0.8", {"start": v(911.61, -139.92) * mm, "end": v(920.9, -139.92) * mm});
            skArc(sketch, "E27.19.0.9", {"start": v(911.61, -139.92) * mm, "mid": v(908.87, -140.73) * mm, "end": v(907.03, -142.92) * mm});
            skPoint(sketch, "E27.19.0.10", {"position": v(927.86, -162.91) * mm});
            skArc(sketch, "E27.19.0.11", {"start": v(925.48, -142.92) * mm, "mid": v(923.63, -140.73) * mm, "end": v(920.9, -139.92) * mm});
            skArc(sketch, "E27.19.0.12", {"start": v(928.3, -156.94) * mm, "mid": v(928.2, -159.93) * mm, "end": v(927.86, -162.91) * mm});
            skArc(sketch, "E27.19.0.13", {"start": v(904.2, -156.94) * mm, "mid": v(904.87, -149.78) * mm, "end": v(907.03, -142.92) * mm});
            skLineSegment(sketch, "E27.direction1", {"start": v(-27.83, -156.92) * mm, "end": v(20.4, -156.92) * mm, "construction": true});
            skLineSegment(sketch, "E28", {"start": v(950.75, -166.04) * mm, "end": v(950.75, -220.54) * mm});
            skArc(sketch, "E29.1.0", {"start": v(72.26, 28.32) * mm, "mid": v(75.08, 29.36) * mm, "end": v(77.66, 30.91) * mm});
            skArc(sketch, "E29.1.1", {"start": v(56.65, 48.9) * mm, "mid": v(58.57, 48.1) * mm, "end": v(60.6, 48.56) * mm});
            skArc(sketch, "E29.1.2", {"start": v(60.55, 48.53) * mm, "mid": v(62.87, 50.45) * mm, "end": v(65.5, 51.91) * mm});
            skLineSegment(sketch, "E29.1.3", {"start": v(88.69, 45.84) * mm, "end": v(86.37, 49.86) * mm});
            skPoint(sketch, "E29.1.4", {"position": v(77.66, 30.91) * mm});
            skPoint(sketch, "E29.1.5", {"position": v(90.24, 43.17) * mm});
            skArc(sketch, "E29.1.6", {"start": v(73.63, 13.74) * mm, "mid": v(72.33, 19.47) * mm, "end": v(70.59, 25.07) * mm});
            skPoint(sketch, "E29.1.7", {"position": v(82.87, 55.93) * mm});
            skLineSegment(sketch, "E29.1.8", {"start": v(86.37, 49.86) * mm, "end": v(84.32, 53.4) * mm});
            skArc(sketch, "E29.1.9", {"start": v(77.66, 30.91) * mm, "mid": v(83.52, 35.07) * mm, "end": v(88.38, 40.38) * mm});
            skArc(sketch, "E29.1.10", {"start": v(65.5, 51.91) * mm, "mid": v(72.4, 54.69) * mm, "end": v(79.72, 55.9) * mm});
            skArc(sketch, "E29.1.11", {"start": v(70.6, 24.91) * mm, "mid": v(70.93, 26.89) * mm, "end": v(72.3, 28.34) * mm});
            skArc(sketch, "E29.1.12", {"start": v(84.32, 53.4) * mm, "mid": v(82.37, 55.3) * mm, "end": v(79.72, 55.9) * mm});
            skLineSegment(sketch, "E29.1.13", {"start": v(84.32, 53.4) * mm, "end": v(86.37, 49.86) * mm, "construction": true});
            skArc(sketch, "E29.1.14", {"start": v(88.38, 40.38) * mm, "mid": v(89.35, 43.06) * mm, "end": v(88.69, 45.84) * mm});
            skArc(sketch, "E29.2.0", {"start": v(48.42, 60.65) * mm, "mid": v(50.34, 62.97) * mm, "end": v(51.8, 65.6) * mm});
            skArc(sketch, "E29.2.1", {"start": v(24.6, 70.68) * mm, "mid": v(26.67, 70.94) * mm, "end": v(28.2, 72.35) * mm});
            skArc(sketch, "E29.2.2", {"start": v(28.17, 72.3) * mm, "mid": v(29.22, 75.13) * mm, "end": v(30.77, 77.7) * mm});
            skLineSegment(sketch, "E29.2.3", {"start": v(53.89, 84.05) * mm, "end": v(49.87, 86.37) * mm});
            skPoint(sketch, "E29.2.4", {"position": v(51.8, 65.6) * mm});
            skPoint(sketch, "E29.2.5", {"position": v(56.56, 82.5) * mm});
            skArc(sketch, "E29.2.6", {"start": v(56.9, 48.72) * mm, "mid": v(52.9, 53.02) * mm, "end": v(48.6, 57) * mm});
            skPoint(sketch, "E29.2.7", {"position": v(43.8, 89.87) * mm});
            skLineSegment(sketch, "E29.2.8", {"start": v(49.87, 86.37) * mm, "end": v(46.32, 88.41) * mm});
            skArc(sketch, "E29.2.9", {"start": v(51.8, 65.6) * mm, "mid": v(54.8, 72.14) * mm, "end": v(56.35, 79.16) * mm});
            skArc(sketch, "E29.2.10", {"start": v(30.77, 77.7) * mm, "mid": v(35.35, 83.56) * mm, "end": v(41.1, 88.27) * mm});
            skArc(sketch, "E29.2.11", {"start": v(48.69, 56.88) * mm, "mid": v(47.98, 58.75) * mm, "end": v(48.44, 60.7) * mm});
            skArc(sketch, "E29.2.12", {"start": v(46.32, 88.41) * mm, "mid": v(43.69, 89.08) * mm, "end": v(41.1, 88.27) * mm});
            skLineSegment(sketch, "E29.2.13", {"start": v(46.32, 88.41) * mm, "end": v(49.87, 86.37) * mm, "construction": true});
            skArc(sketch, "E29.2.14", {"start": v(56.35, 79.16) * mm, "mid": v(55.85, 81.97) * mm, "end": v(53.89, 84.05) * mm});
            skArc(sketch, "E29.3.0", {"start": v(11.6, 76.73) * mm, "mid": v(12.11, 79.7) * mm, "end": v(12.06, 82.71) * mm});
            skArc(sketch, "E29.3.1", {"start": v(-14.03, 73.52) * mm, "mid": v(-12.37, 74.77) * mm, "end": v(-11.75, 76.76) * mm});
            skArc(sketch, "E29.3.2", {"start": v(-11.75, 76.7) * mm, "mid": v(-12.26, 79.67) * mm, "end": v(-12.2, 82.68) * mm});
            skLineSegment(sketch, "E29.3.3", {"start": v(4.64, 99.73) * mm, "end": v(0, 99.73) * mm});
            skPoint(sketch, "E29.3.4", {"position": v(12.06, 82.71) * mm});
            skPoint(sketch, "E29.3.5", {"position": v(7.74, 99.73) * mm});
            skArc(sketch, "E29.3.6", {"start": v(24.92, 70.64) * mm, "mid": v(19.3, 72.37) * mm, "end": v(13.58, 73.67) * mm});
            skPoint(sketch, "E29.3.7", {"position": v(-7, 99.73) * mm});
            skLineSegment(sketch, "E29.3.8", {"start": v(0, 99.73) * mm, "end": v(-4.1, 99.73) * mm});
            skArc(sketch, "E29.3.9", {"start": v(12.06, 82.71) * mm, "mid": v(11.39, 89.87) * mm, "end": v(9.23, 96.73) * mm});
            skArc(sketch, "E29.3.10", {"start": v(-12.2, 82.68) * mm, "mid": v(-11.17, 90.04) * mm, "end": v(-8.55, 97) * mm});
            skArc(sketch, "E29.3.11", {"start": v(13.73, 73.6) * mm, "mid": v(12.18, 74.87) * mm, "end": v(11.6, 76.79) * mm});
            skArc(sketch, "E29.3.12", {"start": v(-4.1, 99.73) * mm, "mid": v(-6.7, 99) * mm, "end": v(-8.55, 97) * mm});
            skLineSegment(sketch, "E29.3.13", {"start": v(-4.1, 99.73) * mm, "end": v(0, 99.73) * mm, "construction": true});
            skArc(sketch, "E29.3.14", {"start": v(9.23, 96.73) * mm, "mid": v(7.38, 98.91) * mm, "end": v(4.64, 99.73) * mm});
            skArc(sketch, "E29.4.0", {"start": v(-28.32, 72.26) * mm, "mid": v(-29.36, 75.08) * mm, "end": v(-30.91, 77.66) * mm});
            skArc(sketch, "E29.4.1", {"start": v(-48.9, 56.65) * mm, "mid": v(-48.1, 58.57) * mm, "end": v(-48.56, 60.6) * mm});
            skArc(sketch, "E29.4.2", {"start": v(-48.53, 60.55) * mm, "mid": v(-50.45, 62.87) * mm, "end": v(-51.91, 65.5) * mm});
            skLineSegment(sketch, "E29.4.3", {"start": v(-45.84, 88.69) * mm, "end": v(-49.86, 86.37) * mm});
            skPoint(sketch, "E29.4.4", {"position": v(-30.91, 77.66) * mm});
            skPoint(sketch, "E29.4.5", {"position": v(-43.17, 90.24) * mm});
            skArc(sketch, "E29.4.6", {"start": v(-13.74, 73.63) * mm, "mid": v(-19.47, 72.33) * mm, "end": v(-25.07, 70.59) * mm});
            skPoint(sketch, "E29.4.7", {"position": v(-55.93, 82.87) * mm});
            skLineSegment(sketch, "E29.4.8", {"start": v(-49.86, 86.37) * mm, "end": v(-53.4, 84.32) * mm});
            skArc(sketch, "E29.4.9", {"start": v(-30.91, 77.66) * mm, "mid": v(-35.07, 83.52) * mm, "end": v(-40.38, 88.38) * mm});
            skArc(sketch, "E29.4.10", {"start": v(-51.91, 65.5) * mm, "mid": v(-54.69, 72.4) * mm, "end": v(-55.9, 79.72) * mm});
            skArc(sketch, "E29.4.11", {"start": v(-24.91, 70.6) * mm, "mid": v(-26.89, 70.93) * mm, "end": v(-28.34, 72.3) * mm});
            skArc(sketch, "E29.4.12", {"start": v(-53.4, 84.32) * mm, "mid": v(-55.3, 82.37) * mm, "end": v(-55.9, 79.72) * mm});
            skLineSegment(sketch, "E29.4.13", {"start": v(-53.4, 84.32) * mm, "end": v(-49.86, 86.37) * mm, "construction": true});
            skArc(sketch, "E29.4.14", {"start": v(-40.38, 88.38) * mm, "mid": v(-43.06, 89.35) * mm, "end": v(-45.84, 88.69) * mm});
            skArc(sketch, "E29.5.0", {"start": v(-60.65, 48.42) * mm, "mid": v(-62.97, 50.34) * mm, "end": v(-65.6, 51.8) * mm});
            skArc(sketch, "E29.5.1", {"start": v(-70.68, 24.6) * mm, "mid": v(-70.94, 26.67) * mm, "end": v(-72.35, 28.2) * mm});
            skArc(sketch, "E29.5.2", {"start": v(-72.3, 28.17) * mm, "mid": v(-75.13, 29.22) * mm, "end": v(-77.7, 30.77) * mm});
            skLineSegment(sketch, "E29.5.3", {"start": v(-84.05, 53.89) * mm, "end": v(-86.37, 49.87) * mm});
            skPoint(sketch, "E29.5.4", {"position": v(-65.6, 51.8) * mm});
            skPoint(sketch, "E29.5.5", {"position": v(-82.5, 56.56) * mm});
            skArc(sketch, "E29.5.6", {"start": v(-48.72, 56.9) * mm, "mid": v(-53.02, 52.9) * mm, "end": v(-57, 48.6) * mm});
            skPoint(sketch, "E29.5.7", {"position": v(-89.87, 43.8) * mm});
            skLineSegment(sketch, "E29.5.8", {"start": v(-86.37, 49.87) * mm, "end": v(-88.41, 46.32) * mm});
            skArc(sketch, "E29.5.9", {"start": v(-65.6, 51.8) * mm, "mid": v(-72.14, 54.8) * mm, "end": v(-79.16, 56.35) * mm});
            skArc(sketch, "E29.5.10", {"start": v(-77.7, 30.77) * mm, "mid": v(-83.56, 35.35) * mm, "end": v(-88.27, 41.1) * mm});
            skArc(sketch, "E29.5.11", {"start": v(-56.88, 48.69) * mm, "mid": v(-58.75, 47.98) * mm, "end": v(-60.7, 48.44) * mm});
            skArc(sketch, "E29.5.12", {"start": v(-88.41, 46.32) * mm, "mid": v(-89.08, 43.69) * mm, "end": v(-88.27, 41.1) * mm});
            skLineSegment(sketch, "E29.5.13", {"start": v(-88.41, 46.32) * mm, "end": v(-86.37, 49.87) * mm, "construction": true});
            skArc(sketch, "E29.5.14", {"start": v(-79.16, 56.35) * mm, "mid": v(-81.97, 55.85) * mm, "end": v(-84.05, 53.89) * mm});
            skArc(sketch, "E29.6.0", {"start": v(-76.73, 11.6) * mm, "mid": v(-79.7, 12.11) * mm, "end": v(-82.71, 12.06) * mm});
            skArc(sketch, "E29.6.1", {"start": v(-73.52, -14.03) * mm, "mid": v(-74.77, -12.37) * mm, "end": v(-76.76, -11.75) * mm});
            skArc(sketch, "E29.6.2", {"start": v(-76.7, -11.75) * mm, "mid": v(-79.67, -12.26) * mm, "end": v(-82.68, -12.2) * mm});
            skLineSegment(sketch, "E29.6.3", {"start": v(-99.73, 4.64) * mm, "end": v(-99.73, 0) * mm});
            skPoint(sketch, "E29.6.4", {"position": v(-82.71, 12.06) * mm});
            skPoint(sketch, "E29.6.5", {"position": v(-99.73, 7.74) * mm});
            skArc(sketch, "E29.6.6", {"start": v(-70.64, 24.92) * mm, "mid": v(-72.37, 19.3) * mm, "end": v(-73.67, 13.58) * mm});
            skPoint(sketch, "E29.6.7", {"position": v(-99.73, -7) * mm});
            skLineSegment(sketch, "E29.6.8", {"start": v(-99.73, 0) * mm, "end": v(-99.73, -4.1) * mm});
            skArc(sketch, "E29.6.9", {"start": v(-82.71, 12.06) * mm, "mid": v(-89.87, 11.39) * mm, "end": v(-96.73, 9.23) * mm});
            skArc(sketch, "E29.6.10", {"start": v(-82.68, -12.2) * mm, "mid": v(-90.04, -11.17) * mm, "end": v(-97, -8.55) * mm});
            skArc(sketch, "E29.6.11", {"start": v(-73.6, 13.73) * mm, "mid": v(-74.87, 12.18) * mm, "end": v(-76.79, 11.6) * mm});
            skArc(sketch, "E29.6.12", {"start": v(-99.73, -4.1) * mm, "mid": v(-99, -6.7) * mm, "end": v(-97, -8.55) * mm});
            skLineSegment(sketch, "E29.6.13", {"start": v(-99.73, -4.1) * mm, "end": v(-99.73, 0) * mm, "construction": true});
            skArc(sketch, "E29.6.14", {"start": v(-96.73, 9.23) * mm, "mid": v(-98.91, 7.38) * mm, "end": v(-99.73, 4.64) * mm});
            skArc(sketch, "E29.7.0", {"start": v(-72.26, -28.32) * mm, "mid": v(-75.08, -29.36) * mm, "end": v(-77.66, -30.91) * mm});
            skArc(sketch, "E29.7.1", {"start": v(-56.65, -48.9) * mm, "mid": v(-58.57, -48.1) * mm, "end": v(-60.6, -48.56) * mm});
            skArc(sketch, "E29.7.2", {"start": v(-60.55, -48.53) * mm, "mid": v(-62.87, -50.45) * mm, "end": v(-65.5, -51.91) * mm});
            skLineSegment(sketch, "E29.7.3", {"start": v(-88.69, -45.84) * mm, "end": v(-86.37, -49.86) * mm});
            skPoint(sketch, "E29.7.4", {"position": v(-77.66, -30.91) * mm});
            skPoint(sketch, "E29.7.5", {"position": v(-90.24, -43.17) * mm});
            skArc(sketch, "E29.7.6", {"start": v(-73.63, -13.74) * mm, "mid": v(-72.33, -19.47) * mm, "end": v(-70.59, -25.07) * mm});
            skPoint(sketch, "E29.7.7", {"position": v(-82.87, -55.93) * mm});
            skLineSegment(sketch, "E29.7.8", {"start": v(-86.37, -49.86) * mm, "end": v(-84.32, -53.4) * mm});
            skArc(sketch, "E29.7.9", {"start": v(-77.66, -30.91) * mm, "mid": v(-83.52, -35.07) * mm, "end": v(-88.38, -40.38) * mm});
            skArc(sketch, "E29.7.10", {"start": v(-65.5, -51.91) * mm, "mid": v(-72.4, -54.69) * mm, "end": v(-79.72, -55.9) * mm});
            skArc(sketch, "E29.7.11", {"start": v(-70.6, -24.91) * mm, "mid": v(-70.93, -26.89) * mm, "end": v(-72.3, -28.34) * mm});
            skArc(sketch, "E29.7.12", {"start": v(-84.32, -53.4) * mm, "mid": v(-82.37, -55.3) * mm, "end": v(-79.72, -55.9) * mm});
            skLineSegment(sketch, "E29.7.13", {"start": v(-84.32, -53.4) * mm, "end": v(-86.37, -49.86) * mm, "construction": true});
            skArc(sketch, "E29.7.14", {"start": v(-88.38, -40.38) * mm, "mid": v(-89.35, -43.06) * mm, "end": v(-88.69, -45.84) * mm});
            skArc(sketch, "E29.8.0", {"start": v(-48.42, -60.65) * mm, "mid": v(-50.34, -62.97) * mm, "end": v(-51.8, -65.6) * mm});
            skArc(sketch, "E29.8.1", {"start": v(-24.6, -70.68) * mm, "mid": v(-26.67, -70.94) * mm, "end": v(-28.2, -72.35) * mm});
            skArc(sketch, "E29.8.2", {"start": v(-28.17, -72.3) * mm, "mid": v(-29.22, -75.13) * mm, "end": v(-30.77, -77.7) * mm});
            skLineSegment(sketch, "E29.8.3", {"start": v(-53.89, -84.05) * mm, "end": v(-49.87, -86.37) * mm});
            skPoint(sketch, "E29.8.4", {"position": v(-51.8, -65.6) * mm});
            skPoint(sketch, "E29.8.5", {"position": v(-56.56, -82.5) * mm});
            skArc(sketch, "E29.8.6", {"start": v(-56.9, -48.72) * mm, "mid": v(-52.9, -53.02) * mm, "end": v(-48.6, -57) * mm});
            skPoint(sketch, "E29.8.7", {"position": v(-43.8, -89.87) * mm});
            skLineSegment(sketch, "E29.8.8", {"start": v(-49.87, -86.37) * mm, "end": v(-46.32, -88.41) * mm});
            skArc(sketch, "E29.8.9", {"start": v(-51.8, -65.6) * mm, "mid": v(-54.8, -72.14) * mm, "end": v(-56.35, -79.16) * mm});
            skArc(sketch, "E29.8.10", {"start": v(-30.77, -77.7) * mm, "mid": v(-35.35, -83.56) * mm, "end": v(-41.1, -88.27) * mm});
            skArc(sketch, "E29.8.11", {"start": v(-48.69, -56.88) * mm, "mid": v(-47.98, -58.75) * mm, "end": v(-48.44, -60.7) * mm});
            skArc(sketch, "E29.8.12", {"start": v(-46.32, -88.41) * mm, "mid": v(-43.69, -89.08) * mm, "end": v(-41.1, -88.27) * mm});
            skLineSegment(sketch, "E29.8.13", {"start": v(-46.32, -88.41) * mm, "end": v(-49.87, -86.37) * mm, "construction": true});
            skArc(sketch, "E29.8.14", {"start": v(-56.35, -79.16) * mm, "mid": v(-55.85, -81.97) * mm, "end": v(-53.89, -84.05) * mm});
            skArc(sketch, "E29.9.0", {"start": v(-11.6, -76.73) * mm, "mid": v(-12.11, -79.7) * mm, "end": v(-12.06, -82.71) * mm});
            skArc(sketch, "E29.9.1", {"start": v(14.03, -73.52) * mm, "mid": v(12.37, -74.77) * mm, "end": v(11.75, -76.76) * mm});
            skArc(sketch, "E29.9.2", {"start": v(11.75, -76.7) * mm, "mid": v(12.26, -79.67) * mm, "end": v(12.2, -82.68) * mm});
            skLineSegment(sketch, "E29.9.3", {"start": v(-4.64, -99.73) * mm, "end": v(0, -99.73) * mm});
            skPoint(sketch, "E29.9.4", {"position": v(-12.06, -82.71) * mm});
            skPoint(sketch, "E29.9.5", {"position": v(-7.74, -99.73) * mm});
            skArc(sketch, "E29.9.6", {"start": v(-24.92, -70.64) * mm, "mid": v(-19.3, -72.37) * mm, "end": v(-13.58, -73.67) * mm});
            skPoint(sketch, "E29.9.7", {"position": v(7, -99.73) * mm});
            skLineSegment(sketch, "E29.9.8", {"start": v(0, -99.73) * mm, "end": v(4.1, -99.73) * mm});
            skArc(sketch, "E29.9.9", {"start": v(-12.06, -82.71) * mm, "mid": v(-11.39, -89.87) * mm, "end": v(-9.23, -96.73) * mm});
            skArc(sketch, "E29.9.10", {"start": v(12.2, -82.68) * mm, "mid": v(11.17, -90.04) * mm, "end": v(8.55, -97) * mm});
            skArc(sketch, "E29.9.11", {"start": v(-13.73, -73.6) * mm, "mid": v(-12.18, -74.87) * mm, "end": v(-11.6, -76.79) * mm});
            skArc(sketch, "E29.9.12", {"start": v(4.1, -99.73) * mm, "mid": v(6.7, -99) * mm, "end": v(8.55, -97) * mm});
            skLineSegment(sketch, "E29.9.13", {"start": v(4.1, -99.73) * mm, "end": v(0, -99.73) * mm, "construction": true});
            skArc(sketch, "E29.9.14", {"start": v(-9.23, -96.73) * mm, "mid": v(-7.38, -98.91) * mm, "end": v(-4.64, -99.73) * mm});
            skArc(sketch, "E29.10.0", {"start": v(28.32, -72.26) * mm, "mid": v(29.36, -75.08) * mm, "end": v(30.91, -77.66) * mm});
            skArc(sketch, "E29.10.1", {"start": v(48.9, -56.65) * mm, "mid": v(48.1, -58.57) * mm, "end": v(48.56, -60.6) * mm});
            skArc(sketch, "E29.10.2", {"start": v(48.53, -60.55) * mm, "mid": v(50.45, -62.87) * mm, "end": v(51.91, -65.5) * mm});
            skLineSegment(sketch, "E29.10.3", {"start": v(45.84, -88.69) * mm, "end": v(49.86, -86.37) * mm});
            skPoint(sketch, "E29.10.4", {"position": v(30.91, -77.66) * mm});
            skPoint(sketch, "E29.10.5", {"position": v(43.17, -90.24) * mm});
            skArc(sketch, "E29.10.6", {"start": v(13.74, -73.63) * mm, "mid": v(19.47, -72.33) * mm, "end": v(25.07, -70.59) * mm});
            skPoint(sketch, "E29.10.7", {"position": v(55.93, -82.87) * mm});
            skLineSegment(sketch, "E29.10.8", {"start": v(49.86, -86.37) * mm, "end": v(53.4, -84.32) * mm});
            skArc(sketch, "E29.10.9", {"start": v(30.91, -77.66) * mm, "mid": v(35.07, -83.52) * mm, "end": v(40.38, -88.38) * mm});
            skArc(sketch, "E29.10.10", {"start": v(51.91, -65.5) * mm, "mid": v(54.69, -72.4) * mm, "end": v(55.9, -79.72) * mm});
            skArc(sketch, "E29.10.11", {"start": v(24.91, -70.6) * mm, "mid": v(26.89, -70.93) * mm, "end": v(28.34, -72.3) * mm});
            skArc(sketch, "E29.10.12", {"start": v(53.4, -84.32) * mm, "mid": v(55.3, -82.37) * mm, "end": v(55.9, -79.72) * mm});
            skLineSegment(sketch, "E29.10.13", {"start": v(53.4, -84.32) * mm, "end": v(49.86, -86.37) * mm, "construction": true});
            skArc(sketch, "E29.10.14", {"start": v(40.38, -88.38) * mm, "mid": v(43.06, -89.35) * mm, "end": v(45.84, -88.69) * mm});
            skArc(sketch, "E29.11.0", {"start": v(60.65, -48.42) * mm, "mid": v(62.97, -50.34) * mm, "end": v(65.6, -51.8) * mm});
            skArc(sketch, "E29.11.1", {"start": v(70.68, -24.6) * mm, "mid": v(70.94, -26.67) * mm, "end": v(72.35, -28.2) * mm});
            skArc(sketch, "E29.11.2", {"start": v(72.3, -28.17) * mm, "mid": v(75.13, -29.22) * mm, "end": v(77.7, -30.77) * mm});
            skLineSegment(sketch, "E29.11.3", {"start": v(84.05, -53.89) * mm, "end": v(86.37, -49.87) * mm});
            skPoint(sketch, "E29.11.4", {"position": v(65.6, -51.8) * mm});
            skPoint(sketch, "E29.11.5", {"position": v(82.5, -56.56) * mm});
            skArc(sketch, "E29.11.6", {"start": v(48.72, -56.9) * mm, "mid": v(53.02, -52.9) * mm, "end": v(57, -48.6) * mm});
            skPoint(sketch, "E29.11.7", {"position": v(89.87, -43.8) * mm});
            skLineSegment(sketch, "E29.11.8", {"start": v(86.37, -49.87) * mm, "end": v(88.41, -46.32) * mm});
            skArc(sketch, "E29.11.9", {"start": v(65.6, -51.8) * mm, "mid": v(72.14, -54.8) * mm, "end": v(79.16, -56.35) * mm});
            skArc(sketch, "E29.11.10", {"start": v(77.7, -30.77) * mm, "mid": v(83.56, -35.35) * mm, "end": v(88.27, -41.1) * mm});
            skArc(sketch, "E29.11.11", {"start": v(56.88, -48.69) * mm, "mid": v(58.75, -47.98) * mm, "end": v(60.7, -48.44) * mm});
            skArc(sketch, "E29.11.12", {"start": v(88.41, -46.32) * mm, "mid": v(89.08, -43.69) * mm, "end": v(88.27, -41.1) * mm});
            skLineSegment(sketch, "E29.11.13", {"start": v(88.41, -46.32) * mm, "end": v(86.37, -49.87) * mm, "construction": true});
            skArc(sketch, "E29.11.14", {"start": v(79.16, -56.35) * mm, "mid": v(81.97, -55.85) * mm, "end": v(84.05, -53.89) * mm});
            skCircle(sketch, "E30", {"center": v(0.03, 0) * mm, "radius": 15 * mm});
            skSolve(sketch);
        }
        {
            var Q0;
            {var subQ9=sQuery(id+"F0.wireOp",EDGE,"E3.2.0");Q0=makeQuery(id+"F0.imprint","IMPRINT",FACE,{"disambiguationData":[TD([[makeQuery(id+"F0.imprint","IMPRINT",EDGE,{"derivedFrom":subQ9}),1.0]])]});}
            var Q1;
            {var subQ4=sQuery(id+"F0.wireOp",EDGE,"43c88bd2-27eb-41b2-b4d7-a541bab70a75.9.1");Q1=makeQuery(id+"F0.imprint","IMPRINT",FACE,{"disambiguationData":[TD([[makeQuery(id+"F0.imprint","IMPRINT",EDGE,{"derivedFrom":subQ4}),1.0]])]});}
            var Q2;
            {var subQ4=sQuery(id+"F0.wireOp",EDGE,"43c88bd2-27eb-41b2-b4d7-a541bab70a75.8.1");Q2=makeQuery(id+"F0.imprint","IMPRINT",FACE,{"disambiguationData":[TD([[makeQuery(id+"F0.imprint","IMPRINT",EDGE,{"derivedFrom":subQ4}),1.0]])]});}
            var Q3;
            {var subQ6=sQuery(id+"F0.wireOp",EDGE,"43c88bd2-27eb-41b2-b4d7-a541bab70a75.7.1");Q3=makeQuery(id+"F0.imprint","IMPRINT",FACE,{"disambiguationData":[TD([[makeQuery(id+"F0.imprint","IMPRINT",EDGE,{"derivedFrom":subQ6}),1.0]])]});}
            var Q4;
            {var subQ6=sQuery(id+"F0.wireOp",EDGE,"43c88bd2-27eb-41b2-b4d7-a541bab70a75.6.1");Q4=makeQuery(id+"F0.imprint","IMPRINT",FACE,{"disambiguationData":[TD([[makeQuery(id+"F0.imprint","IMPRINT",EDGE,{"derivedFrom":subQ6}),1.0]])]});}
            var Q5;
            {var subQ6=sQuery(id+"F0.wireOp",EDGE,"43c88bd2-27eb-41b2-b4d7-a541bab70a75.5.1");Q5=makeQuery(id+"F0.imprint","IMPRINT",FACE,{"disambiguationData":[TD([[makeQuery(id+"F0.imprint","IMPRINT",EDGE,{"derivedFrom":subQ6}),1.0]])]});}
            var Q6;
            {var subQ6=sQuery(id+"F0.wireOp",EDGE,"43c88bd2-27eb-41b2-b4d7-a541bab70a75.4.1");Q6=makeQuery(id+"F0.imprint","IMPRINT",FACE,{"disambiguationData":[TD([[makeQuery(id+"F0.imprint","IMPRINT",EDGE,{"derivedFrom":subQ6}),1.0]])]});}
            var Q7;
            {var subQ6=sQuery(id+"F0.wireOp",EDGE,"43c88bd2-27eb-41b2-b4d7-a541bab70a75.3.1");Q7=makeQuery(id+"F0.imprint","IMPRINT",FACE,{"disambiguationData":[TD([[makeQuery(id+"F0.imprint","IMPRINT",EDGE,{"derivedFrom":subQ6}),1.0]])]});}
            var Q8;
            {var subQ6=sQuery(id+"F0.wireOp",EDGE,"43c88bd2-27eb-41b2-b4d7-a541bab70a75.2.1");Q8=makeQuery(id+"F0.imprint","IMPRINT",FACE,{"disambiguationData":[TD([[makeQuery(id+"F0.imprint","IMPRINT",EDGE,{"derivedFrom":subQ6}),1.0]])]});}
            var Q9;
            {var subQ6=sQuery(id+"F0.wireOp",EDGE,"43c88bd2-27eb-41b2-b4d7-a541bab70a75.1.1");Q9=makeQuery(id+"F0.imprint","IMPRINT",FACE,{"disambiguationData":[TD([[makeQuery(id+"F0.imprint","IMPRINT",EDGE,{"derivedFrom":subQ6}),1.0]])]});}
            var Q10;
            Q10=makeQuery(id+"F0.imprint","IMPRINT",FACE,{"disambiguationData":[TD([[makeQuery(id+"F0.imprint","IMPRINT",EDGE,{"derivedFrom":sQuery(id+"F0.wireOp",EDGE,"E0")}),1.0]])]});
            var Q11;
            {var subQ4=sQuery(id+"F0.wireOp",EDGE,"43c88bd2-27eb-41b2-b4d7-a541bab70a75.11.1");Q11=makeQuery(id+"F0.imprint","IMPRINT",FACE,{"disambiguationData":[TD([[makeQuery(id+"F0.imprint","IMPRINT",EDGE,{"derivedFrom":subQ4}),1.0]])]});}
            extrude(context, id + "F1", {"entities" : qUnion([Q0, Q1, Q2, Q3, Q4, Q5, Q6, Q7, Q8, Q9, Q10, Q11]), "depth" : 50 * mm});
        }
        {
            var Q0;
            Q0=makeQuery(id+"F0.imprint","IMPRINT",FACE,{"disambiguationData":[TD([[makeQuery(id+"F0.imprint","IMPRINT",EDGE,{"derivedFrom":sQuery(id+"F0.wireOp",EDGE,"E9.2.MirrorCS")}),-1.0]])]});
            extrude(context, id + "F2", {"entities" : qUnion([Q0]), "depth" : 50 * mm});
        }
        {
            var Q0;
            Q0=makeQuery(id+"F2.opExtrude","SWEPT_FACE",FACE,{"disambiguationData":[OSD([sQuery(id+"F0.wireOp",EDGE,"E28")])]});
            var sketch = newSketch(context, id + "F3", { "sketchPlane" : qUnion([Q0])});
            skLineSegment(sketch, "E31", {"start": v(-166.04, 50) * mm, "end": v(-166.04, 75) * mm, "construction": true});
            skLineSegment(sketch, "E32", {"start": v(-166.04, 0) * mm, "end": v(-166.04, -25) * mm});
            skLineSegment(sketch, "E33.top", {"start": v(-261.37, 75) * mm, "end": v(-166.04, 75) * mm});
            skLineSegment(sketch, "E33.right", {"start": v(-166.04, 50) * mm, "end": v(-166.04, 75) * mm});
            skLineSegment(sketch, "E34.top", {"start": v(-220.54, 50) * mm, "end": v(-166.04, 50) * mm});
            skLineSegment(sketch, "E35.0.MirrorCS", {"start": v(-220.54, 0) * mm, "end": v(-166.04, 0) * mm});
            skLineSegment(sketch, "E36.0.MirrorCS", {"start": v(-261.37, -25) * mm, "end": v(-166.04, -25) * mm});
            skPoint(sketch, "E37.start.orphan", {"position": v(-166.04, 25) * mm});
            skPoint(sketch, "E34.left.start.orphan", {"position": v(-220.54, 25) * mm});
            skLineSegment(sketch, "E38", {"start": v(-220.54, 50) * mm, "end": v(-220.54, 0) * mm});
            skLineSegment(sketch, "E39.trimOffspring", {"start": v(-166.04, 0) * mm, "end": v(-166.04, -25) * mm, "construction": true});
            skLineSegment(sketch, "E40", {"start": v(-261.37, 75) * mm, "end": v(-261.37, -25) * mm});
            skPoint(sketch, "E41.visualSharp", {"position": v(-166.04, 75) * mm});
            skLineSegment(sketch, "E41.filletArc", {"start": v(-166.04, 75) * mm, "end": v(-166.04, 75) * mm});
            skPoint(sketch, "E42.visualSharp", {"position": v(-166.04, -25) * mm});
            skLineSegment(sketch, "E42.filletArc", {"start": v(-166.04, -25) * mm, "end": v(-166.04, -25) * mm});
            skSolve(sketch);
        }
        {
            var Q0;
            Q0=makeQuery(id+"F3.imprint","IMPRINT",FACE,{"disambiguationData":[TD([[makeQuery(id+"F3.imprint","IMPRINT",EDGE,{"derivedFrom":sQuery(id+"F3.wireOp",EDGE,"E32")}),-1.0]])]});
            extrude(context, id + "F4", {"entities" : qUnion([Q0]), "oppositeDirection" : true, "depth" : 2000 * mm});
        }
        {
            var Q0;
            Q0=makeQuery(id+"F4.opExtrude","SWEPT_FACE",FACE,{"disambiguationData":[OSD([sQuery(id+"F3.wireOp",EDGE,"E33.right")])]});
            var sketch = newSketch(context, id + "F5", { "sketchPlane" : qUnion([Q0])});
            skLineSegment(sketch, "E43.bottom", {"start": v(-100.75, 75) * mm, "end": v(199.25, 75) * mm});
            skLineSegment(sketch, "E43.top", {"start": v(-100.75, 50) * mm, "end": v(199.25, 50) * mm});
            skLineSegment(sketch, "E43.left", {"start": v(-100.75, 75) * mm, "end": v(-100.75, 50) * mm});
            skLineSegment(sketch, "E43.right", {"start": v(199.25, 75) * mm, "end": v(199.25, 50) * mm});
            skLineSegment(sketch, "E44.bottom", {"start": v(-100.75, 0) * mm, "end": v(199.25, 0) * mm});
            skLineSegment(sketch, "E44.top", {"start": v(-100.75, -25) * mm, "end": v(199.25, -25) * mm, "construction": true});
            skLineSegment(sketch, "E44.left", {"start": v(-100.75, 0) * mm, "end": v(-100.75, -25) * mm});
            skLineSegment(sketch, "E44.right", {"start": v(199.25, 0) * mm, "end": v(199.25, -25) * mm});
            skLineSegment(sketch, "E45", {"start": v(199.25, 50) * mm, "end": v(199.24, 0.15) * mm, "construction": true});
            skLineSegment(sketch, "E46", {"start": v(-100.75, 50) * mm, "end": v(-100.75, 0) * mm, "construction": true});
            skLineSegment(sketch, "E47.top", {"start": v(-100.75, -25) * mm, "end": v(199.25, -25) * mm});
            skSolve(sketch);
        }
        {
            var Q0;
            Q0=makeQuery(id+"F5.imprint","IMPRINT",FACE,{"disambiguationData":[TD([[makeQuery(id+"F5.imprint","IMPRINT",EDGE,{"derivedFrom":sQuery(id+"F5.wireOp",EDGE,"E43.bottom")}),1.0]])]});
            var Q1;
            Q1=makeQuery(id+"F5.imprint","IMPRINT",FACE,{"disambiguationData":[TD([[makeQuery(id+"F5.imprint","IMPRINT",EDGE,{"derivedFrom":sQuery(id+"F5.wireOp",EDGE,"E44.bottom")}),-1.0]])]});
            extrude(context, id + "F6", {"entities" : qUnion([Q0, Q1]), "operationType" : NewBodyOperationType.ADD, "depth" : 155 * mm});
        }
        {
            var Q0;
            Q0=makeQuery(id+"F6.boolean.opBoolean","MERGE",FACE,{"derivedFrom":[makeQuery(id+"F4.opExtrude","SWEPT_FACE",FACE,{"disambiguationData":[OSD([sQuery(id+"F3.wireOp",EDGE,"E36.0.MirrorCS")])]}),makeQuery(id+"F6.opExtrude","SWEPT_FACE",FACE,{"disambiguationData":[OSD([sQuery(id+"F5.wireOp",EDGE,"E47.top")])]})]});
            var sketch = newSketch(context, id + "F7", { "sketchPlane" : qUnion([Q0])});
            skLineSegment(sketch, "E48", {"start": v(-49.25, 161.04) * mm, "end": v(-49.25, 61.04) * mm, "construction": true});
            skArc(sketch, "E49", {"start": v(-88.02, 29.47) * mm, "mid": v(-49.25, 11.04) * mm, "end": v(-10.48, 29.47) * mm});
            skLineSegment(sketch, "E50", {"start": v(-199.25, 166.04) * mm, "end": v(-88.02, 29.47) * mm});
            skLineSegment(sketch, "E51", {"start": v(100.75, 166.04) * mm, "end": v(-10.48, 29.47) * mm});
            skCircle(sketch, "E52", {"center": v(-49.25, 61.04) * mm, "radius": 15 * mm});
            skLineSegment(sketch, "E53", {"start": v(-199.25, 166.04) * mm, "end": v(100.75, 166.04) * mm, "construction": true});
            skArc(sketch, "E54", {"start": v(-12.4, 94.85) * mm, "mid": v(-49.25, 111.04) * mm, "end": v(-86.1, 94.85) * mm});
            skLineSegment(sketch, "E55", {"start": v(-99.33, 111.53) * mm, "end": v(-142.58, 166.04) * mm});
            skLineSegment(sketch, "E56", {"start": v(-142.58, 166.04) * mm, "end": v(44.08, 166.04) * mm});
            skLineSegment(sketch, "E57.1.MirrorCS", {"start": v(0.83, 111.53) * mm, "end": v(44.08, 166.04) * mm});
            skLineSegment(sketch, "E58", {"start": v(0.83, 111.53) * mm, "end": v(-12.4, 94.85) * mm});
            skLineSegment(sketch, "E59", {"start": v(-99.33, 111.53) * mm, "end": v(-86.1, 94.85) * mm});
            skArc(sketch, "E60.trimOffspring", {"start": v(-88.02, 29.47) * mm, "mid": v(-49.25, 11.04) * mm, "end": v(-10.48, 29.47) * mm, "construction": true});
            skPoint(sketch, "E57.0.MirrorCS.start.orphan", {"position": v(-49.25, 111.04) * mm});
            skSolve(sketch);
        }
        {
            var Q0;
            {var subQ5=sQuery(id+"F7.wireOp",EDGE,"E51");Q0=makeQuery(id+"F7.imprint","IMPRINT",FACE,{"disambiguationData":[TD([[makeQuery(id+"F7.imprint","IMPRINT",EDGE,{"derivedFrom":subQ5}),1.0]])]});}
            var Q1;
            {var subQ5=sQuery(id+"F7.wireOp",EDGE,"E50");Q1=makeQuery(id+"F7.imprint","IMPRINT",FACE,{"disambiguationData":[TD([[makeQuery(id+"F7.imprint","IMPRINT",EDGE,{"derivedFrom":subQ5}),-1.0]])]});}
            var Q2;
            Q2=makeQuery(id+"F7.imprint","IMPRINT",FACE,{"disambiguationData":[TD([[makeQuery(id+"F7.imprint","IMPRINT",EDGE,{"derivedFrom":sQuery(id+"F7.wireOp",EDGE,"E54")}),-1.0]])]});
            var Q3;
            Q3=makeQuery(id+"F7.imprint","IMPRINT",FACE,{"disambiguationData":[TD([[makeQuery(id+"F7.imprint","IMPRINT",EDGE,{"derivedFrom":sQuery(id+"F7.wireOp",EDGE,"E52")}),1.0]])]});
            extrude(context, id + "F8", {"entities" : qUnion([Q0, Q1, Q2, Q3]), "operationType" : NewBodyOperationType.REMOVE, "endBound" : BoundingType.THROUGH_ALL, "oppositeDirection" : true, "depth" : 25 * mm});
        }
        {
            var Q0;
            Q0=makeQuery(id+"F7.imprint","IMPRINT",FACE,{"disambiguationData":[TD([[makeQuery(id+"F7.imprint","IMPRINT",EDGE,{"derivedFrom":sQuery(id+"F7.wireOp",EDGE,"E52")}),1.0]])]});
            extrude(context, id + "F9", {"entities" : qUnion([Q0]), "oppositeDirection" : true, "depth" : 100 * mm});
        }
    });
